# Revit family: IS_Idealrain_Multiproduct_BIM_DE_B9400;B9401
name_source: partatom
category: Plumbing Fixtures
revit_build: Autodesk Revit MEP 2016 (Build: 20161004_0715(x64)
units: mm (PartAtom-declared; Revit-internal decimal feet)

## family parameters
Cut with Voids When Loaded = No
Host = Face
OmniClass Number = 23.45.55.17
OmniClass Title = Mixing Faucets
Part Type = Normal
Room Calculation Point = No
Round Connector Dimension = Use Diameter
Shared = Yes

## types (2) — shared parameters
Accessories = www.idealstandard.de\ersatzteile
AreaUnits = millimeters
Assembly Code = C1030200
AssetType = Fixed
BIMObjectName = ISI_IdealStandard_MixerTaps_IDEALRAIN_B9400AA
BarCode = 3800861023111
Brand = Ideal Standard
CodePerformance = 0
Color = Chrome
ConnectionType = Mechanical
CurrencyUnit = €
Default Elevation = 800 mm  [stored 2.62467 ft]
Description = Idealrain S1 Hand Spray 1F  80Mm
DurationUnit = year
ExpectedLife = 25
FaucetFunction = MIXED
FaucetOperation = LEVERHANDLE
FaucetType = PILLAR
Features = IDEALRAIN single function handspray 80mm
Finish = Chrome
FlowRate = 8 L/min @ 3 bar
GrossWeight = 0,215 kg
IfcExportAs = IfcValveType
IfcExportType = FAUCET
InstallationDate = 1900-12-31T23:59:59
InstallationInstructions = www.idealstandard.de\produkte
LinearUnits = millimeters
ManufacturerURL = www.idealstandard.de
Material = Brass
Model = B9400AA
ModelNumber = B9400AA
ModelReference = IS 1-Funktionshandbrause IDEALRAIN, d:80mm, Chrom
NBSDescription = Shower fittings package
NBSReference = 45-35-70/330
Name = ISI_IdealStandard_MixerTaps_IDEALRAIN_B9400AA
NettWeight = 0,13 kg
NominalHeight = 210 mm
NominalLength = 106 mm
NominalWidth = 80 mm
ProductInformation = www.idealstandard.de
Shape = Sculptured
Size = 210 x 106 x 80 mm
Space = Internal
SpareParts = www.idealstandard.de/ersatzteile
TestPressure = 10 Bar
URL = www.idealstandard.de
Uniclass2015Code = Pr_40_20_87_75
Uniclass2015Title = Shower fittings package
Uniclass2015Version = Products v1.1
Version = 1
VolumeUnits = Litres
WorkingPressure = 1-5 Bar
zero-valued in all types: CWFU, Cost, HWFU, NominalDepth, WFU

## per-type parameters (varying)
| type | B9401 |
| B9400AA - IDEALRAIN S1 H/SPRAY 1F CHROME 80MM | No |
| B9401AA - IDEALRAIN S3 H/SPRAY 3F CHROME 80MM | Yes |

note: [stored X ft] marks values corroborated as IEEE doubles in the binary element streams (Revit-internal decimal feet)

## geometry (parser evidence)
native form markers: Blend x4, Sweep x1
no freeform markers — native parametric forms only
